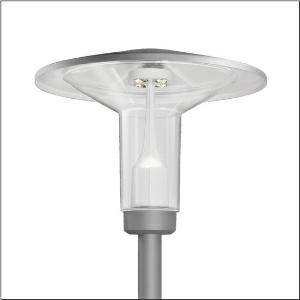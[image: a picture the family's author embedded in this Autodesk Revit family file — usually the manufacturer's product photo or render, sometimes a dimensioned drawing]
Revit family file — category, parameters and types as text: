
# Revit family: laterne_iq___p1_0a_5xa5255bf14h_d88c
name_source: partatom
category: Lighting Fixtures
units: mm (PartAtom-declared; Revit-internal decimal feet)

## family parameters
Cut with Voids When Loaded = No
Host = Face
Light Source = No
Part Type = Normal
Room Calculation Point = No
Round Connector Dimension = Use Diameter
Shared = No

## types (1)
- --- (1 x LED, 1510 lm, 12.9 W, 2200K)
    Apparent Load = 13 VA
    CIE Flux Codes = 35 64 91 96 100
    Color Rendering = 70
    Color Temperature = 2200K
    Default Elevation = 1800 mm
    Description = Lantern iQ, mast luminaire, Module 540 iQ-SR, primary light control with 3 zone facetted reflector, of plastic, silver coated, highly specular, structured, primary optical cover: cover, of PMMA, transparent, light distribution: P1.0a, light emission: direct distribution, primary light characteristic: strongly asymmetric, installation type: post-top, LED, High Power LED, rated luminous flux: 1.510lm, luminous efficacy: 117lm/W, light colour: 722, colour temperature: 2200K, control gear: ECG iQ, control: presetting dimming logarithmic, Street-Remote, Auto-Match, Temp-Guard, Lumen-Switch, Night-Set, Smart-Wire, Light-Fading, Desk-Remote (wireless, voltage-free reading and setting of iQ features in the workshop via application-optimized NFC function/RFID function), optimised constant luminous flux control (CLO 2.0), with terminal, 6-pole, max. 2.5mm², mains connection: 230..240V, AC, 50/60Hz, start of lifetime: 13W, end of service life: 13W, reduction: 6W, luminaire housing, upper part, of glass-fibre reinforced polyester, coated, Siteco® metallic grey (DB 702S), diameter: 750mm, height: 583mm, spigot size: d x l = 76 x 70mm (post-top) | with reducer (optional accessory) 60 x 70mm, post-top mast mounting element, of diecast aluminium, coated, Siteco® metallic grey (DB 702S), Module 540 iQ-SR, traffic white (RAL 9016), equipment: standard, protection rating (complete): IP65, insulation class (complete): insulation class II (safety insulation), certification: CE, ENEC, VDE, packaging unit: 1 piece

Light Distribution: P1.0a
    Height = 583 mm
    Lamp = 1 x LED
    Lamp Light Flux = 1510 lm
    Lamp Power = 12.9 W
    Lamp count = 1
    Length = 750 mm
    Luminous efficacy = 117 lm/W
    Manufacturer = Siteco
    ModVariant = No
    Model = 5XA5255BF14H
    Number of Poles = 1
    OnlyDefault = Yes
    Power Factor = 1
    Product Name = Laterne iQ | P1.0a
    Product group = mast luminaire | pylon top
    ProductGroupID = 6100
    Protection Class = Protection class II
    Protection Degree = IP 65
    RLX_Detail_Level = 1
    RLX_Emergency_Light_Flux = 0 lm
    RLX_Emergency_Type = 0
    RLX_Emergency_Type_DB = No
    RlxData = <blob elided: 74049 chars, md5=616dc086>
    Socket = socket
    Standby Power = 0 W
    System Light Flux = 1510 lm
    System Power = 13 W
    Type Comments = factory setting: luminous flux: 100 % | dim-lin: 254 | 516 mA
    Type Image = l_1006050.jpg
    URL = http://relux.com
    VarID = @adj_110713
    Voltage = 0 V
    Weight = 0.00 kg
    Width = 0 mm  [stored 0 ft]

note: [stored X ft] marks values corroborated as IEEE doubles in the binary element streams (Revit-internal decimal feet)

## geometry (parser evidence)
native form markers: Blend x4, Sweep x9
no freeform markers — native parametric forms only
